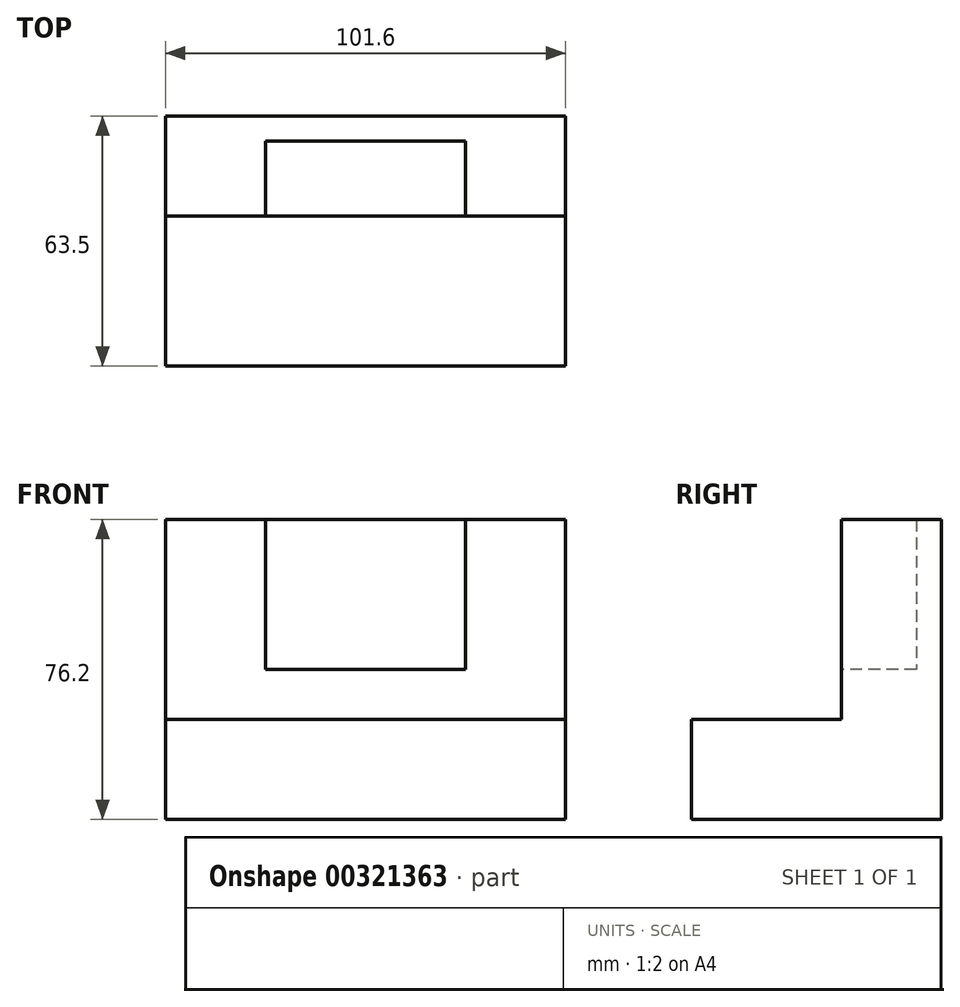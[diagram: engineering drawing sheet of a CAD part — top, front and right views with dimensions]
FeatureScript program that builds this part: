
annotation { "Feature Type Name" : "Feature", "Feature Type Description" : "" }
export const myFeature = defineFeature(function(context is Context, id is Id, definition is map)
    precondition{}
    {
        {
            var Q0;
            Q0=qCreatedBy(makeId("Right.planeOp"),FACE);
            var sketch = newSketch(context, id + "F0", { "sketchPlane" : qUnion([Q0])});
            skLineSegment(sketch, "E0", {"start": v(-16.2, -40.52) * mm, "end": v(47.3, -40.52) * mm});
            skLineSegment(sketch, "E1", {"start": v(47.3, -40.52) * mm, "end": v(47.3, 35.68) * mm});
            skLineSegment(sketch, "E2", {"start": v(47.3, 35.68) * mm, "end": v(21.9, 35.68) * mm});
            skLineSegment(sketch, "E3", {"start": v(21.9, 35.68) * mm, "end": v(21.9, -15.12) * mm});
            skLineSegment(sketch, "E4", {"start": v(21.9, -15.12) * mm, "end": v(-16.2, -15.12) * mm});
            skLineSegment(sketch, "E5", {"start": v(-16.2, -15.12) * mm, "end": v(-16.2, -40.52) * mm});
            skSolve(sketch);
        }
        {
            var Q0;
            Q0 = qSketchRegion(id + "F0", true);
            var Q1;
            Q1=makeQuery(id+"F0.imprint","IMPRINT",FACE,{"disambiguationData":[TD([[makeQuery(id+"F0.imprint","IMPRINT",EDGE,{"derivedFrom":sQuery(id+"F0.wireOp",EDGE,"E0")}),1.0]])]});
            extrude(context, id + "F1", {"entities" : qUnion([Q0, Q1]), "oppositeDirection" : true, "depth" : 101.6 * mm});
        }
        {
            var Q0;
            Q0=makeQuery(id+"F1.opExtrude","SWEPT_FACE",FACE,{"disambiguationData":[OSD([sQuery(id+"F0.wireOp",EDGE,"E3")])]});
            var sketch = newSketch(context, id + "F2", { "sketchPlane" : qUnion([Q0])});
            skLineSegment(sketch, "E6.bottom", {"start": v(-76.2, 35.68) * mm, "end": v(-25.4, 35.68) * mm});
            skLineSegment(sketch, "E6.top", {"start": v(-76.2, -2.42) * mm, "end": v(-25.4, -2.42) * mm});
            skLineSegment(sketch, "E6.left", {"start": v(-76.2, 35.68) * mm, "end": v(-76.2, -2.42) * mm});
            skLineSegment(sketch, "E6.right", {"start": v(-25.4, 35.68) * mm, "end": v(-25.4, -2.42) * mm});
            skSolve(sketch);
        }
        {
            var Q0;
            Q0=makeQuery(id+"F2.imprint","IMPRINT",FACE,{"disambiguationData":[TD([[makeQuery(id+"F2.imprint","IMPRINT",EDGE,{"derivedFrom":sQuery(id+"F2.wireOp",EDGE,"E6.bottom")}),-1.0]])]});
            extrude(context, id + "F3", {"entities" : qUnion([Q0]), "operationType" : NewBodyOperationType.REMOVE, "oppositeDirection" : true, "depth" : 19.05 * mm});
        }
    });
